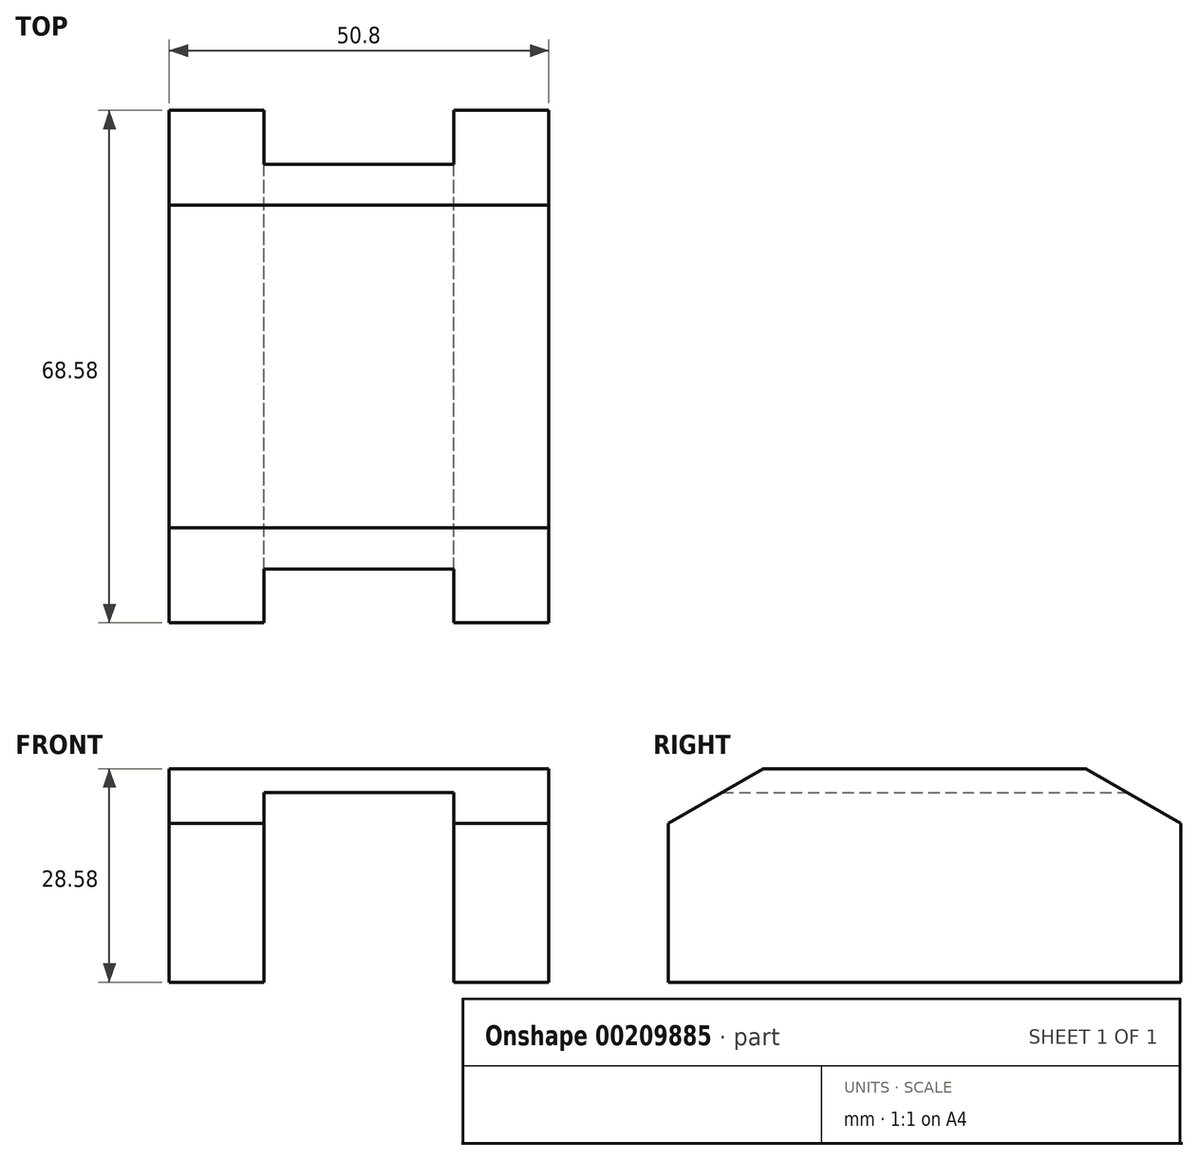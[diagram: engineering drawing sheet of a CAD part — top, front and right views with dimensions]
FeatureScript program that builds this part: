
annotation { "Feature Type Name" : "Feature", "Feature Type Description" : "" }
export const myFeature = defineFeature(function(context is Context, id is Id, definition is map)
    precondition{}
    {
        {
            var Q0;
            Q0=qCreatedBy(makeId("Front.planeOp"),FACE);
            var sketch = newSketch(context, id + "F0", { "sketchPlane" : qUnion([Q0])});
            skLineSegment(sketch, "E0.bottom", {"start": v(0, 0) * mm, "end": v(-50.8, 0) * mm});
            skLineSegment(sketch, "E0.top", {"start": v(0, 28.57) * mm, "end": v(-50.8, 28.57) * mm});
            skLineSegment(sketch, "E0.left", {"start": v(0, 0) * mm, "end": v(0, 28.57) * mm});
            skLineSegment(sketch, "E0.right", {"start": v(-50.8, 0) * mm, "end": v(-50.8, 28.57) * mm});
            skLineSegment(sketch, "E1.bottom", {"start": v(-38.1, 0) * mm, "end": v(-12.7, 0) * mm, "construction": true});
            skLineSegment(sketch, "E1.top", {"start": v(-38.1, 25.4) * mm, "end": v(-12.7, 25.4) * mm});
            skLineSegment(sketch, "E1.left", {"start": v(-38.1, 0) * mm, "end": v(-38.1, 25.4) * mm});
            skLineSegment(sketch, "E1.right", {"start": v(-12.7, 0) * mm, "end": v(-12.7, 25.4) * mm});
            skSolve(sketch);
        }
        {
            var Q0;
            Q0=makeQuery(id+"F0.imprint","IMPRINT",FACE,{"disambiguationData":[TD([[makeQuery(id+"F0.imprint","IMPRINT",EDGE,{"derivedFrom":sQuery(id+"F0.wireOp",EDGE,"E0.top")}),1.0]])]});
            extrude(context, id + "F1", {"entities" : qUnion([Q0]), "depth" : 68.58 * mm});
        }
        {
            var Q0;
            Q0=makeQuery(id+"F1.opExtrude","CAP_EDGE",EDGE,{"disambiguationData":[OSD([sQuery(id+"F0.wireOp",EDGE,"E0.top")])],"isStart":true});
            var Q1;
            Q1=makeQuery(id+"F1.opExtrude","CAP_EDGE",EDGE,{"disambiguationData":[OSD([sQuery(id+"F0.wireOp",EDGE,"E0.top")])],"isStart":false});
            chamfer(context, id + "F2", {"entities" : qUnion([Q0, Q1]), "chamferType" : ChamferType.OFFSET_ANGLE, "width" : 12.7 * mm, "oppositeDirection" : false, "angle" : 30 * degree, "tangentPropagation" : true});
        }
    });
